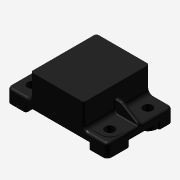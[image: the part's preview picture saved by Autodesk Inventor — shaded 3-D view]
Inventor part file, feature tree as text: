
AUTODESK INVENTOR PART (.ipt)
format: ipt  version: 2016 SP1 (Build 200210100, 210)  size: 485,888 bytes
history: native  units: mm (DEFAULTED — no unit token found)
features: sketch x12, extrude x11, fillet x5, mirror x3, plane x2, rib x1
ambient origin geometry x8: Origin, YZ Plane, XZ Plane, XY Plane, X Axis, Y Axis, Z Axis, Center Point
bodies: Solid1 (feature_tree)
feature tree (34):
  extrude  "Extrusion1"  Depth=5.08mm
  fillet  "Fillet19"  Radius=73.66mm
  extrude  "Extrusion4"  Depth=48.26mm TaperAngle=0.0deg
  fillet  "Fillet20"  Radius=3.048mm
  extrude  "Extrusion10"  Depth=1.524mm
  extrude  "Extrusion12"  Depth=10.16mm
  fillet  "Fillet21"  Radius=8.255mm
  plane  "Work Plane3"
  plane  "Work Plane4"
  mirror  "Mirror4"
  mirror  "Mirror5"
  extrude  "Extrusion11"  Depth=0.381mm TaperAngle=0.0deg
  extrude  "Extrusion13"  Depth=3.302mm
  extrude  "Extrusion14"  Depth=8.636mm
  extrude  "Extrusion15"  Depth=2.54mm
  extrude  "Extrusion16"  Depth=0.762mm
  extrude  "Extrusion5"  Depth=3.048mm
  extrude  "Extrusion6"  Depth=13.97mm
  rib  "Rib2"
  fillet  "Fillet22"  Radius=16.51mm
  fillet  "Fillet23"  Radius=4.826mm
  mirror  "Mirror6"
  sketch  "Sketch1"  dims[d1=23.099032mm d2=5.08mm d3=73.66mm]
  sketch  "Sketch5"  dims[d4=38.862mm d5=48.26mm d6=0.0mm d40=3.048mm]
  sketch  "Sketch6"  dims[d41=3.048mm d42=1.524mm]
  sketch  "Sketch7"  dims[d43=6.858mm d44=10.16mm d45=8.255mm]
  sketch  "Sketch8"  dims[d46=8.89mm d47=0.0mm d48=0.381mm d49=0.0mm]
  sketch  "Sketch14"  dims[d50=0.381mm d51=0.0mm d52=3.302mm]
  sketch  "Sketch15"  dims[d53=3.302mm d54=8.636mm]
  sketch  "Sketch16"  dims[d55=3.302mm d56=2.54mm]
  sketch  "Sketch17"  dims[d57=2.54mm d58=0.762mm]
  sketch  "Sketch18"  dims[d59=0.762mm d83=3.048mm]
  sketch  "Sketch19"  dims[d84=1.524mm d85=13.97mm d86=16.51mm d87=4.826mm d88=0.0mm]
  sketch  "Sketch20"  dims[d89=1.27mm d90=4.826mm d91=0.0mm d92=3.048mm d93=1.524mm d94=16.51mm d95=13.97mm d96=4.826mm d97=0.0mm d98=1.27mm d99=4.826mm d100=0.0mm d101=13.97mm d102=13.97mm d103=3.048mm d104=1.524mm d105=1.016mm d106=3.048mm d107=1.524mm d108=1.016mm d109=13.97mm d110=4.826mm d111=0.0mm d112=1.27mm d113=1.27mm d114=0.381mm d116=0.381mm d117=13.97mm d118=4.826mm d119=0.0mm d120=1.27mm d121=0.381mm d122=0.381mm d124=13.97mm d125=4.826mm d126=0.0mm]
